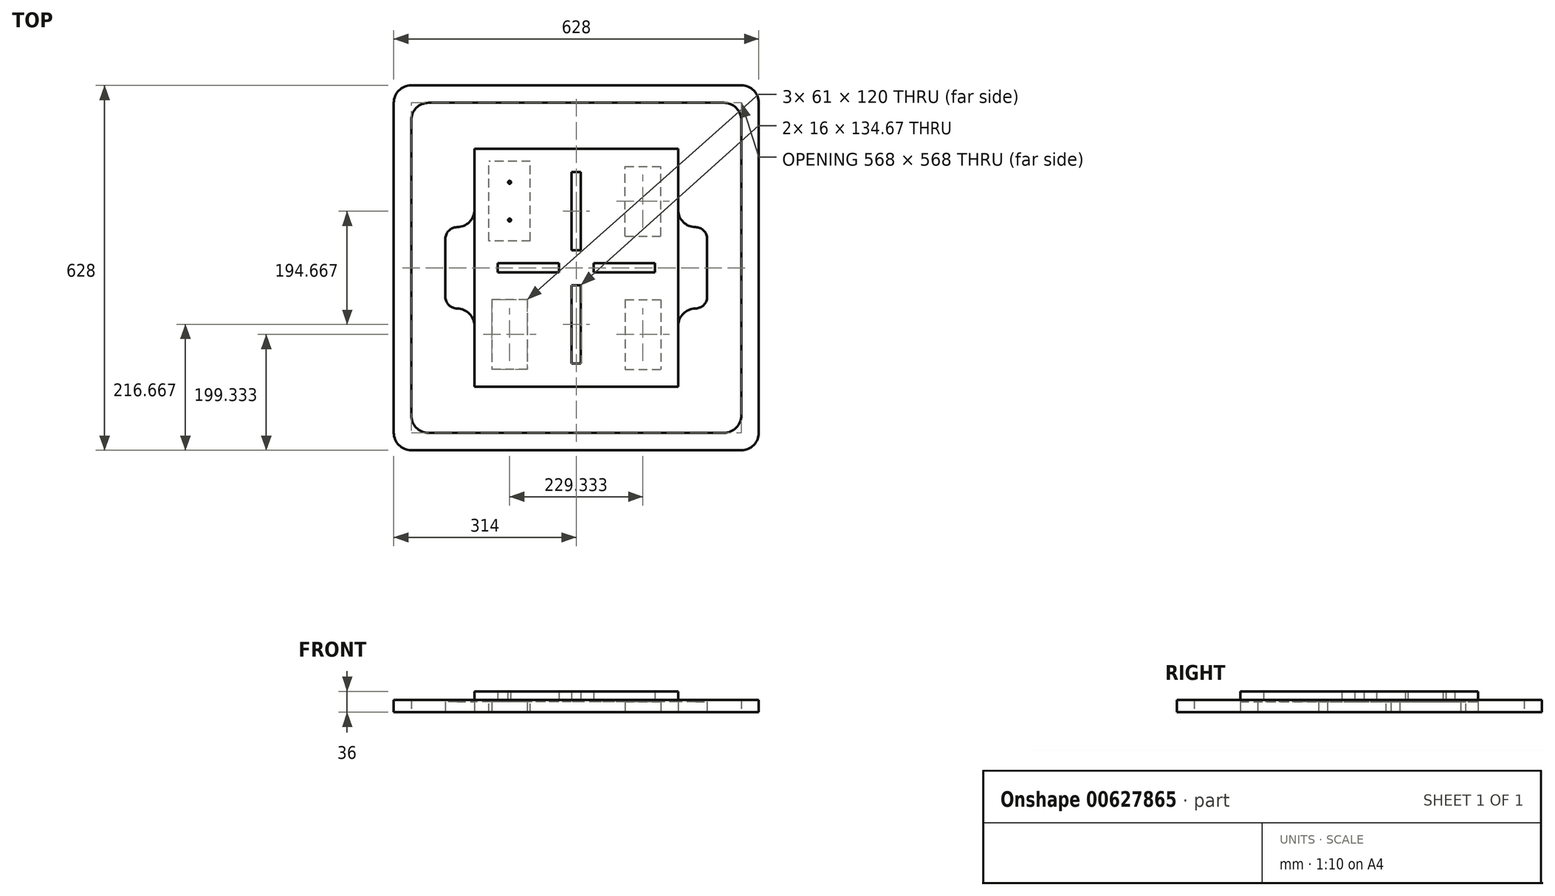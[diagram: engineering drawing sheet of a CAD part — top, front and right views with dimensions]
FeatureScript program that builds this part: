
annotation { "Feature Type Name" : "Feature", "Feature Type Description" : "" }
export const myFeature = defineFeature(function(context is Context, id is Id, definition is map)
    precondition{}
    {
        {
            var Q0;
            Q0=qCreatedBy(makeId("Top.planeOp"),FACE);
            var sketch = newSketch(context, id + "F0", { "sketchPlane" : qUnion([Q0])});
            skLineSegment(sketch, "E0.bottom", {"start": v(314, -314) * mm, "end": v(-314, -314) * mm});
            skLineSegment(sketch, "E0.top", {"start": v(314, 314) * mm, "end": v(-314, 314) * mm});
            skLineSegment(sketch, "E0.left", {"start": v(314, -314) * mm, "end": v(314, 314) * mm});
            skLineSegment(sketch, "E0.right", {"start": v(-314, -314) * mm, "end": v(-314, 314) * mm});
            skPoint(sketch, "E0.middle", {"position": v(0, 0) * mm});
            skLineSegment(sketch, "E1.0", {"start": v(284, 284) * mm, "end": v(-284, 284) * mm});
            skLineSegment(sketch, "E1.1", {"start": v(284, -284) * mm, "end": v(284, 284) * mm});
            skLineSegment(sketch, "E1.2", {"start": v(284, -284) * mm, "end": v(-284, -284) * mm});
            skLineSegment(sketch, "E1.3", {"start": v(-284, -284) * mm, "end": v(-284, 284) * mm});
            skSolve(sketch);
        }
        {
            var Q0;
            Q0=makeQuery(id+"F0.imprint","IMPRINT",FACE,{"disambiguationData":[TD([[makeQuery(id+"F0.imprint","IMPRINT",EDGE,{"derivedFrom":sQuery(id+"F0.wireOp",EDGE,"E0.bottom")}),-1.0]])]});
            extrude(context, id + "F1", {"entities" : qUnion([Q0]), "depth" : 21 * mm, "offsetDistance" : 25 * mm});
        }
        {
            var Q0;
            Q0=makeQuery(id+"F1.opExtrude","SWEPT_EDGE",EDGE,{"disambiguationData":[OSD([sQuery(id+"F0.wireOp",EDGE,"E1.0"),sQuery(id+"F0.wireOp",EDGE,"E1.3")])]});
            var Q1;
            Q1=makeQuery(id+"F1.opExtrude","SWEPT_EDGE",EDGE,{"disambiguationData":[OSD([sQuery(id+"F0.wireOp",EDGE,"E1.0"),sQuery(id+"F0.wireOp",EDGE,"E1.1")])]});
            var Q2;
            Q2=makeQuery(id+"F1.opExtrude","SWEPT_EDGE",EDGE,{"disambiguationData":[OSD([sQuery(id+"F0.wireOp",EDGE,"E1.1"),sQuery(id+"F0.wireOp",EDGE,"E1.2")])]});
            var Q3;
            Q3=makeQuery(id+"F1.opExtrude","SWEPT_EDGE",EDGE,{"disambiguationData":[OSD([sQuery(id+"F0.wireOp",EDGE,"E1.2"),sQuery(id+"F0.wireOp",EDGE,"E1.3")])]});
            fillet(context, id + "F2", {"entities" : qUnion([Q0, Q1, Q2, Q3]), "radius" : 30 * mm, "tangentPropagation" : true, "allowEdgeOverflow" : false});
        }
        {
            var Q0;
            Q0=makeQuery(id+"F1.opExtrude","SWEPT_EDGE",EDGE,{"disambiguationData":[OSD([sQuery(id+"F0.wireOp",EDGE,"E0.bottom"),sQuery(id+"F0.wireOp",EDGE,"E0.right")])]});
            var Q1;
            Q1=makeQuery(id+"F1.opExtrude","SWEPT_EDGE",EDGE,{"disambiguationData":[OSD([sQuery(id+"F0.wireOp",EDGE,"E0.bottom"),sQuery(id+"F0.wireOp",EDGE,"E0.left")])]});
            var Q2;
            Q2=makeQuery(id+"F1.opExtrude","SWEPT_EDGE",EDGE,{"disambiguationData":[OSD([sQuery(id+"F0.wireOp",EDGE,"E0.top"),sQuery(id+"F0.wireOp",EDGE,"E0.left")])]});
            var Q3;
            Q3=makeQuery(id+"F1.opExtrude","SWEPT_EDGE",EDGE,{"disambiguationData":[OSD([sQuery(id+"F0.wireOp",EDGE,"E0.top"),sQuery(id+"F0.wireOp",EDGE,"E0.right")])]});
            fillet(context, id + "F3", {"entities" : qUnion([Q0, Q1, Q2, Q3]), "radius" : 30 * mm, "tangentPropagation" : true, "allowEdgeOverflow" : false});
        }
        {
            var Q0;
            Q0=qCreatedBy(makeId("Top.planeOp"),FACE);
            var sketch = newSketch(context, id + "F4", { "sketchPlane" : qUnion([Q0])});
            skLineSegment(sketch, "E2.bottom", {"start": v(373.17, 373.17) * mm, "end": v(-373.17, 373.17) * mm, "construction": true});
            skLineSegment(sketch, "E2.top", {"start": v(373.17, -373.17) * mm, "end": v(-373.17, -373.17) * mm, "construction": true});
            skLineSegment(sketch, "E2.left", {"start": v(-373.17, -373.17) * mm, "end": v(-373.17, 373.17) * mm, "construction": true});
            skLineSegment(sketch, "E2.right", {"start": v(373.17, -373.17) * mm, "end": v(373.17, 373.17) * mm, "construction": true});
            skPoint(sketch, "E2.middle", {"position": v(0, 0) * mm});
            skLineSegment(sketch, "E3.bottom", {"start": v(-84.17, 54.67) * mm, "end": v(-145.17, 54.67) * mm});
            skLineSegment(sketch, "E3.top", {"start": v(-84.17, 174.67) * mm, "end": v(-145.17, 174.67) * mm});
            skLineSegment(sketch, "E3.left", {"start": v(-84.17, 54.67) * mm, "end": v(-84.17, 174.67) * mm});
            skLineSegment(sketch, "E3.right", {"start": v(-145.17, 54.67) * mm, "end": v(-145.17, 174.67) * mm});
            skPoint(sketch, "E3.middle", {"position": v(-114.67, 114.67) * mm});
            skLineSegment(sketch, "E4", {"start": v(-373.17, 373.17) * mm, "end": v(373.17, -373.17) * mm, "construction": true});
            skLineSegment(sketch, "E5", {"start": v(373.17, 373.17) * mm, "end": v(-373.17, -373.17) * mm, "construction": true});
            skLineSegment(sketch, "E6", {"start": v(0, -373.17) * mm, "end": v(0, 0) * mm, "construction": true});
            skLineSegment(sketch, "E7.MirrorCS", {"start": v(84.17, 54.67) * mm, "end": v(84.17, 174.67) * mm});
            skLineSegment(sketch, "E8.MirrorCS", {"start": v(84.17, 174.67) * mm, "end": v(145.17, 174.67) * mm});
            skLineSegment(sketch, "E9.MirrorCS", {"start": v(145.17, 54.67) * mm, "end": v(145.17, 174.67) * mm});
            skLineSegment(sketch, "E10.MirrorCS", {"start": v(84.17, 54.67) * mm, "end": v(145.17, 54.67) * mm});
            skLineSegment(sketch, "E11", {"start": v(373.17, 0) * mm, "end": v(0, 0) * mm, "construction": true});
            skLineSegment(sketch, "E12.MirrorCS", {"start": v(-84.17, -54.67) * mm, "end": v(-145.17, -54.67) * mm});
            skLineSegment(sketch, "E13.MirrorCS", {"start": v(-145.17, -54.67) * mm, "end": v(-145.17, -174.67) * mm});
            skLineSegment(sketch, "E14.MirrorCS", {"start": v(-84.17, -174.67) * mm, "end": v(-145.17, -174.67) * mm});
            skLineSegment(sketch, "E15.MirrorCS", {"start": v(-84.17, -54.67) * mm, "end": v(-84.17, -174.67) * mm});
            skLineSegment(sketch, "E16.MirrorCS", {"start": v(84.17, -54.67) * mm, "end": v(145.17, -54.67) * mm});
            skLineSegment(sketch, "E17.MirrorCS", {"start": v(84.17, -54.67) * mm, "end": v(84.17, -174.67) * mm});
            skLineSegment(sketch, "E18.MirrorCS", {"start": v(84.17, -174.67) * mm, "end": v(145.17, -174.67) * mm});
            skLineSegment(sketch, "E19.MirrorCS", {"start": v(145.17, -54.67) * mm, "end": v(145.17, -174.67) * mm});
            skLineSegment(sketch, "E20", {"start": v(-114.67, 174.67) * mm, "end": v(-114.67, 284) * mm, "construction": true});
            skLineSegment(sketch, "E21", {"start": v(-145.17, 114.67) * mm, "end": v(-284, 114.67) * mm, "construction": true});
            skLineSegment(sketch, "E22", {"start": v(-84.17, 114.67) * mm, "end": v(84.17, 114.67) * mm, "construction": true});
            skLineSegment(sketch, "E23", {"start": v(145.17, 114.67) * mm, "end": v(284, 114.67) * mm, "construction": true});
            skPoint(sketch, "E23.endSnap0", {"position": v(145.17, 114.67) * mm});
            skLineSegment(sketch, "E24", {"start": v(-114.67, 54.67) * mm, "end": v(-114.67, -54.67) * mm});
            skLineSegment(sketch, "E25.bottom", {"start": v(175.17, -204.67) * mm, "end": v(-175.17, -204.67) * mm});
            skLineSegment(sketch, "E25.top", {"start": v(175.17, 204.67) * mm, "end": v(-175.17, 204.67) * mm});
            skLineSegment(sketch, "E25.left", {"start": v(175.17, -204.67) * mm, "end": v(175.17, -100) * mm});
            skLineSegment(sketch, "E25.right", {"start": v(-175.17, -204.67) * mm, "end": v(-175.17, -100) * mm});
            skLineSegment(sketch, "E26", {"start": v(205.17, 70) * mm, "end": v(205.17, 70) * mm});
            skLineSegment(sketch, "E27", {"start": v(225.17, 50) * mm, "end": v(225.17, 0) * mm});
            skArc(sketch, "E28", {"start": v(175.17, 100) * mm, "mid": v(183.95, 78.79) * mm, "end": v(205.17, 70) * mm});
            skPoint(sketch, "E29.visualSharp", {"position": v(225.17, 70) * mm});
            skArc(sketch, "E29.filletArc", {"start": v(225.17, 50) * mm, "mid": v(219.3, 64.14) * mm, "end": v(205.17, 70) * mm});
            skLineSegment(sketch, "E30.MirrorCS", {"start": v(225.17, -50) * mm, "end": v(225.17, 0) * mm});
            skArc(sketch, "E31.MirrorCS", {"start": v(225.17, -50) * mm, "mid": v(219.3, -64.14) * mm, "end": v(205.17, -70) * mm});
            skArc(sketch, "E32.MirrorCS", {"start": v(175.17, -100) * mm, "mid": v(183.95, -78.79) * mm, "end": v(205.17, -70) * mm});
            skArc(sketch, "E33.MirrorCS", {"start": v(-175.17, -100) * mm, "mid": v(-183.95, -78.79) * mm, "end": v(-205.17, -70) * mm});
            skArc(sketch, "E34.MirrorCS", {"start": v(-225.17, -50) * mm, "mid": v(-219.3, -64.14) * mm, "end": v(-205.17, -70) * mm});
            skLineSegment(sketch, "E35.MirrorCS", {"start": v(-225.17, -50) * mm, "end": v(-225.17, 0) * mm});
            skLineSegment(sketch, "E36.MirrorCS", {"start": v(-225.17, 50) * mm, "end": v(-225.17, 0) * mm});
            skArc(sketch, "E37.MirrorCS", {"start": v(-225.17, 50) * mm, "mid": v(-219.3, 64.14) * mm, "end": v(-205.17, 70) * mm});
            skArc(sketch, "E38.MirrorCS", {"start": v(-175.17, 100) * mm, "mid": v(-183.95, 78.79) * mm, "end": v(-205.17, 70) * mm});
            skLineSegment(sketch, "E39.trimOffspring", {"start": v(-175.17, 100) * mm, "end": v(-175.17, 204.67) * mm});
            skLineSegment(sketch, "E40.trimOffspring", {"start": v(175.17, 100) * mm, "end": v(175.17, 204.67) * mm});
            skSolve(sketch);
        }
        {
            var Q0;
            Q0=makeQuery(id+"F4.imprint","IMPRINT",FACE,{"disambiguationData":[TD([[makeQuery(id+"F4.imprint","IMPRINT",EDGE,{"derivedFrom":sQuery(id+"F4.wireOp",EDGE,"E3.top")}),-1.0]])]});
            extrude(context, id + "F5", {"entities" : qUnion([Q0]), "depth" : 18 * mm, "offsetDistance" : 25 * mm});
        }
        {
            var Q0;
            Q0=makeQuery(id+"F5.opExtrude","CAP_FACE",FACE,{"disambiguationData":[OSD([sQuery(id+"F4.wireOp",EDGE,"E3.bottom"),sQuery(id+"F4.wireOp",EDGE,"E3.top"),sQuery(id+"F4.wireOp",EDGE,"E3.left"),sQuery(id+"F4.wireOp",EDGE,"E3.right"),sQuery(id+"F4.wireOp",EDGE,"E7.MirrorCS"),sQuery(id+"F4.wireOp",EDGE,"E8.MirrorCS"),sQuery(id+"F4.wireOp",EDGE,"E9.MirrorCS"),sQuery(id+"F4.wireOp",EDGE,"E10.MirrorCS"),sQuery(id+"F4.wireOp",EDGE,"E12.MirrorCS"),sQuery(id+"F4.wireOp",EDGE,"E13.MirrorCS"),sQuery(id+"F4.wireOp",EDGE,"E14.MirrorCS"),sQuery(id+"F4.wireOp",EDGE,"E15.MirrorCS"),sQuery(id+"F4.wireOp",EDGE,"E16.MirrorCS"),sQuery(id+"F4.wireOp",EDGE,"E17.MirrorCS"),sQuery(id+"F4.wireOp",EDGE,"E18.MirrorCS"),sQuery(id+"F4.wireOp",EDGE,"E19.MirrorCS"),sQuery(id+"F4.wireOp",EDGE,"E25.bottom"),sQuery(id+"F4.wireOp",EDGE,"E25.top"),sQuery(id+"F4.wireOp",EDGE,"E25.left"),sQuery(id+"F4.wireOp",EDGE,"E25.right"),sQuery(id+"F4.wireOp",EDGE,"E27"),sQuery(id+"F4.wireOp",EDGE,"E28"),sQuery(id+"F4.wireOp",EDGE,"E29.filletArc"),sQuery(id+"F4.wireOp",EDGE,"E30.MirrorCS"),sQuery(id+"F4.wireOp",EDGE,"E31.MirrorCS"),sQuery(id+"F4.wireOp",EDGE,"E32.MirrorCS"),sQuery(id+"F4.wireOp",EDGE,"E33.MirrorCS"),sQuery(id+"F4.wireOp",EDGE,"E34.MirrorCS"),sQuery(id+"F4.wireOp",EDGE,"E35.MirrorCS"),sQuery(id+"F4.wireOp",EDGE,"E36.MirrorCS"),sQuery(id+"F4.wireOp",EDGE,"E37.MirrorCS"),sQuery(id+"F4.wireOp",EDGE,"E38.MirrorCS"),sQuery(id+"F4.wireOp",EDGE,"E39.trimOffspring"),sQuery(id+"F4.wireOp",EDGE,"E40.trimOffspring")])],"isStart":false});
            var sketch = newSketch(context, id + "F6", { "sketchPlane" : qUnion([Q0])});
            skLineSegment(sketch, "E41.bottom", {"start": v(-79.17, 46.17) * mm, "end": v(-150.17, 46.17) * mm});
            skLineSegment(sketch, "E41.top", {"start": v(-79.17, 183.17) * mm, "end": v(-150.17, 183.17) * mm});
            skLineSegment(sketch, "E41.left", {"start": v(-79.17, 46.17) * mm, "end": v(-79.17, 183.17) * mm});
            skLineSegment(sketch, "E41.right", {"start": v(-150.17, 46.17) * mm, "end": v(-150.17, 183.17) * mm});
            skPoint(sketch, "E41.middle", {"position": v(-114.67, 114.67) * mm});
            skPoint(sketch, "E41.middle.positionSnap0", {"position": v(-114.67, 174.67) * mm});
            skPoint(sketch, "E41.centerSnap0", {"position": v(-114.67, 174.67) * mm});
            skSolve(sketch);
        }
        {
            var Q0;
            Q0=makeQuery(id+"F6.imprint","IMPRINT",FACE,{"disambiguationData":[TD([[makeQuery(id+"F6.imprint","IMPRINT",EDGE,{"derivedFrom":sQuery(id+"F6.wireOp",EDGE,"E41.bottom")}),-1.0]])]});
            extrude(context, id + "F7", {"entities" : qUnion([Q0]), "operationType" : NewBodyOperationType.REMOVE, "endBound" : BoundingType.THROUGH_ALL, "oppositeDirection" : true, "depth" : 25 * mm, "offsetDistance" : 25 * mm});
        }
        {
            var Q0;
            Q0=makeQuery(id+"F5.opExtrude","CAP_FACE",FACE,{"disambiguationData":[OSD([sQuery(id+"F4.wireOp",EDGE,"E3.bottom"),sQuery(id+"F4.wireOp",EDGE,"E3.top"),sQuery(id+"F4.wireOp",EDGE,"E3.left"),sQuery(id+"F4.wireOp",EDGE,"E3.right"),sQuery(id+"F4.wireOp",EDGE,"E7.MirrorCS"),sQuery(id+"F4.wireOp",EDGE,"E8.MirrorCS"),sQuery(id+"F4.wireOp",EDGE,"E9.MirrorCS"),sQuery(id+"F4.wireOp",EDGE,"E10.MirrorCS"),sQuery(id+"F4.wireOp",EDGE,"E12.MirrorCS"),sQuery(id+"F4.wireOp",EDGE,"E13.MirrorCS"),sQuery(id+"F4.wireOp",EDGE,"E14.MirrorCS"),sQuery(id+"F4.wireOp",EDGE,"E15.MirrorCS"),sQuery(id+"F4.wireOp",EDGE,"E16.MirrorCS"),sQuery(id+"F4.wireOp",EDGE,"E17.MirrorCS"),sQuery(id+"F4.wireOp",EDGE,"E18.MirrorCS"),sQuery(id+"F4.wireOp",EDGE,"E19.MirrorCS"),sQuery(id+"F4.wireOp",EDGE,"E25.bottom"),sQuery(id+"F4.wireOp",EDGE,"E25.top"),sQuery(id+"F4.wireOp",EDGE,"E25.left"),sQuery(id+"F4.wireOp",EDGE,"E25.right"),sQuery(id+"F4.wireOp",EDGE,"E27"),sQuery(id+"F4.wireOp",EDGE,"E28"),sQuery(id+"F4.wireOp",EDGE,"E29.filletArc"),sQuery(id+"F4.wireOp",EDGE,"E30.MirrorCS"),sQuery(id+"F4.wireOp",EDGE,"E31.MirrorCS"),sQuery(id+"F4.wireOp",EDGE,"E32.MirrorCS"),sQuery(id+"F4.wireOp",EDGE,"E33.MirrorCS"),sQuery(id+"F4.wireOp",EDGE,"E34.MirrorCS"),sQuery(id+"F4.wireOp",EDGE,"E35.MirrorCS"),sQuery(id+"F4.wireOp",EDGE,"E36.MirrorCS"),sQuery(id+"F4.wireOp",EDGE,"E37.MirrorCS"),sQuery(id+"F4.wireOp",EDGE,"E38.MirrorCS"),sQuery(id+"F4.wireOp",EDGE,"E39.trimOffspring"),sQuery(id+"F4.wireOp",EDGE,"E40.trimOffspring")])],"isStart":false});
            var sketch = newSketch(context, id + "F8", { "sketchPlane" : qUnion([Q0])});
            skLineSegment(sketch, "E42.bottom", {"start": v(175.17, -204.67) * mm, "end": v(-175.17, -204.67) * mm});
            skLineSegment(sketch, "E42.top", {"start": v(175.17, 204.67) * mm, "end": v(-175.17, 204.67) * mm});
            skLineSegment(sketch, "E42.left", {"start": v(175.17, -204.67) * mm, "end": v(175.17, 204.67) * mm});
            skLineSegment(sketch, "E42.right", {"start": v(-175.17, -204.67) * mm, "end": v(-175.17, 204.67) * mm});
            skPoint(sketch, "E42.middle", {"position": v(0, 0) * mm});
            skLineSegment(sketch, "E43.bottom", {"start": v(8, 164.67) * mm, "end": v(-8, 164.67) * mm});
            skLineSegment(sketch, "E43.top", {"start": v(8, -164.67) * mm, "end": v(-8, -164.67) * mm});
            skLineSegment(sketch, "E43.left", {"start": v(8, 164.67) * mm, "end": v(8, 30) * mm});
            skLineSegment(sketch, "E43.right", {"start": v(-8, 164.67) * mm, "end": v(-8, 30) * mm});
            skLineSegment(sketch, "E44.bottom", {"start": v(135.17, -8) * mm, "end": v(30, -8) * mm});
            skLineSegment(sketch, "E44.top", {"start": v(135.17, 8) * mm, "end": v(30, 8) * mm});
            skLineSegment(sketch, "E44.left", {"start": v(135.17, -8) * mm, "end": v(135.17, 8) * mm});
            skLineSegment(sketch, "E44.right", {"start": v(-135.17, -8) * mm, "end": v(-135.17, 8) * mm});
            skLineSegment(sketch, "E45.bottom", {"start": v(8, -30) * mm, "end": v(-8, -30) * mm});
            skLineSegment(sketch, "E45.top", {"start": v(8, 30) * mm, "end": v(-8, 30) * mm});
            skLineSegment(sketch, "E45.left", {"start": v(30, -8) * mm, "end": v(30, 8) * mm});
            skLineSegment(sketch, "E45.right", {"start": v(-30, -8) * mm, "end": v(-30, 8) * mm});
            skPoint(sketch, "E46.orphan", {"position": v(30, 30) * mm});
            skPoint(sketch, "E47.orphan", {"position": v(-30, -30) * mm});
            skPoint(sketch, "E48.orphan", {"position": v(-30, 30) * mm});
            skPoint(sketch, "E49.orphan", {"position": v(30, -30) * mm});
            skLineSegment(sketch, "E50.trimOffspring", {"start": v(-8, 8) * mm, "end": v(-8, -8) * mm, "construction": true});
            skLineSegment(sketch, "E51.trimOffspring", {"start": v(8, 8) * mm, "end": v(8, -8) * mm, "construction": true});
            skLineSegment(sketch, "E52.trimOffspring", {"start": v(-30, 8) * mm, "end": v(-135.17, 8) * mm});
            skLineSegment(sketch, "E53.trimOffspring", {"start": v(-30, -8) * mm, "end": v(-135.17, -8) * mm});
            skLineSegment(sketch, "E54.trimOffspring", {"start": v(8, 8) * mm, "end": v(-8, 8) * mm, "construction": true});
            skLineSegment(sketch, "E55.trimOffspring", {"start": v(8, -8) * mm, "end": v(-8, -8) * mm, "construction": true});
            skLineSegment(sketch, "E56.trimOffspring", {"start": v(-8, -30) * mm, "end": v(-8, -164.67) * mm});
            skLineSegment(sketch, "E57.trimOffspring", {"start": v(8, -30) * mm, "end": v(8, -164.67) * mm});
            skSolve(sketch);
        }
        {
            var Q0;
            Q0 = qSketchRegion(id + "F8", true);
            extrude(context, id + "F9", {"entities" : qUnion([Q0]), "depth" : 18 * mm, "offsetDistance" : 25 * mm});
        }
        {
            var Q0;
            Q0=makeQuery(id+"F9.opExtrude","CAP_FACE",FACE,{"disambiguationData":[OSD([sQuery(id+"F8.wireOp",EDGE,"E42.bottom"),sQuery(id+"F8.wireOp",EDGE,"E42.top"),sQuery(id+"F8.wireOp",EDGE,"E42.left"),sQuery(id+"F8.wireOp",EDGE,"E42.right"),sQuery(id+"F8.wireOp",EDGE,"E43.bottom"),sQuery(id+"F8.wireOp",EDGE,"E43.top"),sQuery(id+"F8.wireOp",EDGE,"E43.left"),sQuery(id+"F8.wireOp",EDGE,"E43.right"),sQuery(id+"F8.wireOp",EDGE,"E44.bottom"),sQuery(id+"F8.wireOp",EDGE,"E44.top"),sQuery(id+"F8.wireOp",EDGE,"E44.left"),sQuery(id+"F8.wireOp",EDGE,"E44.right"),sQuery(id+"F8.wireOp",EDGE,"E45.bottom"),sQuery(id+"F8.wireOp",EDGE,"E45.top"),sQuery(id+"F8.wireOp",EDGE,"E45.left"),sQuery(id+"F8.wireOp",EDGE,"E45.right"),sQuery(id+"F8.wireOp",EDGE,"E52.trimOffspring"),sQuery(id+"F8.wireOp",EDGE,"E53.trimOffspring"),sQuery(id+"F8.wireOp",EDGE,"E56.trimOffspring"),sQuery(id+"F8.wireOp",EDGE,"E57.trimOffspring")])],"isStart":false});
            var sketch = newSketch(context, id + "F10", { "sketchPlane" : qUnion([Q0])});
            skCircle(sketch, "E58", {"center": v(-114.67, 147.17) * mm, "radius": 2.5 * mm});
            skCircle(sketch, "E59", {"center": v(-114.67, 82.17) * mm, "radius": 2.5 * mm});
            skLineSegment(sketch, "E60", {"start": v(-114.67, 147.17) * mm, "end": v(-114.67, 82.17) * mm, "construction": true});
            skLineSegment(sketch, "E61", {"start": v(-114.67, 114.67) * mm, "end": v(-100.01, 114.67) * mm, "construction": true});
            skLineSegment(sketch, "E62.bottom", {"start": v(-91.17, 58.17) * mm, "end": v(-138.17, 58.17) * mm, "construction": true});
            skLineSegment(sketch, "E62.top", {"start": v(-91.17, 171.17) * mm, "end": v(-138.17, 171.17) * mm, "construction": true});
            skLineSegment(sketch, "E62.left", {"start": v(-91.17, 58.17) * mm, "end": v(-91.17, 171.17) * mm, "construction": true});
            skLineSegment(sketch, "E62.right", {"start": v(-138.17, 58.17) * mm, "end": v(-138.17, 171.17) * mm, "construction": true});
            skPoint(sketch, "E62.middle", {"position": v(-114.67, 114.67) * mm});
            skSolve(sketch);
        }
        {
            var Q0;
            Q0 = qSketchRegion(id + "F10", true);
            extrude(context, id + "F11", {"entities" : qUnion([Q0]), "operationType" : NewBodyOperationType.REMOVE, "endBound" : BoundingType.THROUGH_ALL, "oppositeDirection" : true, "depth" : 25 * mm, "offsetDistance" : 25 * mm});
        }
    });
